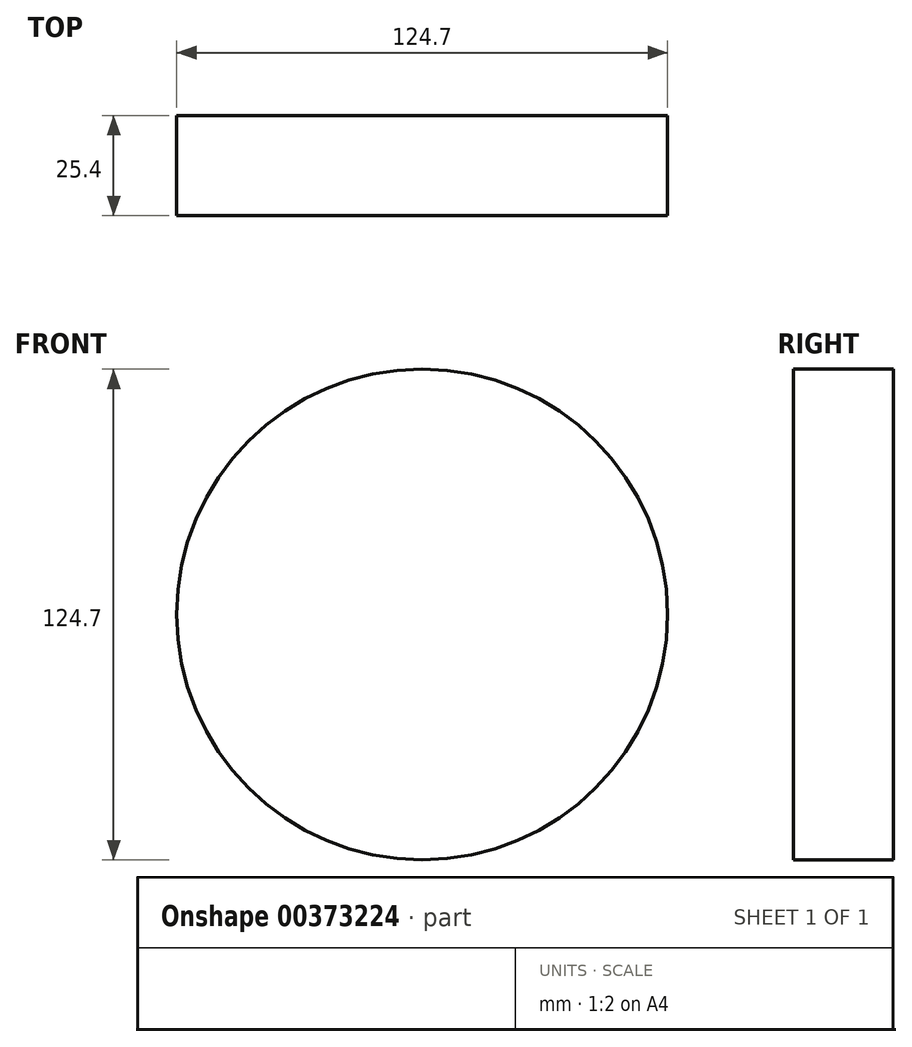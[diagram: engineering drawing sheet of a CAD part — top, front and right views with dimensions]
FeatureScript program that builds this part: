
annotation { "Feature Type Name" : "Feature", "Feature Type Description" : "" }
export const myFeature = defineFeature(function(context is Context, id is Id, definition is map)
    precondition{}
    {
        {
            var Q0;
            Q0=qCreatedBy(makeId("Front.planeOp"),FACE);
            var sketch = newSketch(context, id + "F0", { "sketchPlane" : qUnion([Q0])});
            skCircle(sketch, "E0", {"center": v(0, 0) * mm, "radius": 62.35 * mm});
            skSolve(sketch);
        }
        {
            var Q0;
            Q0 = qSketchRegion(id + "F0", true);
            extrude(context, id + "F1", {"entities" : qUnion([Q0]), "depth" : 25.4 * mm});
        }
    });
